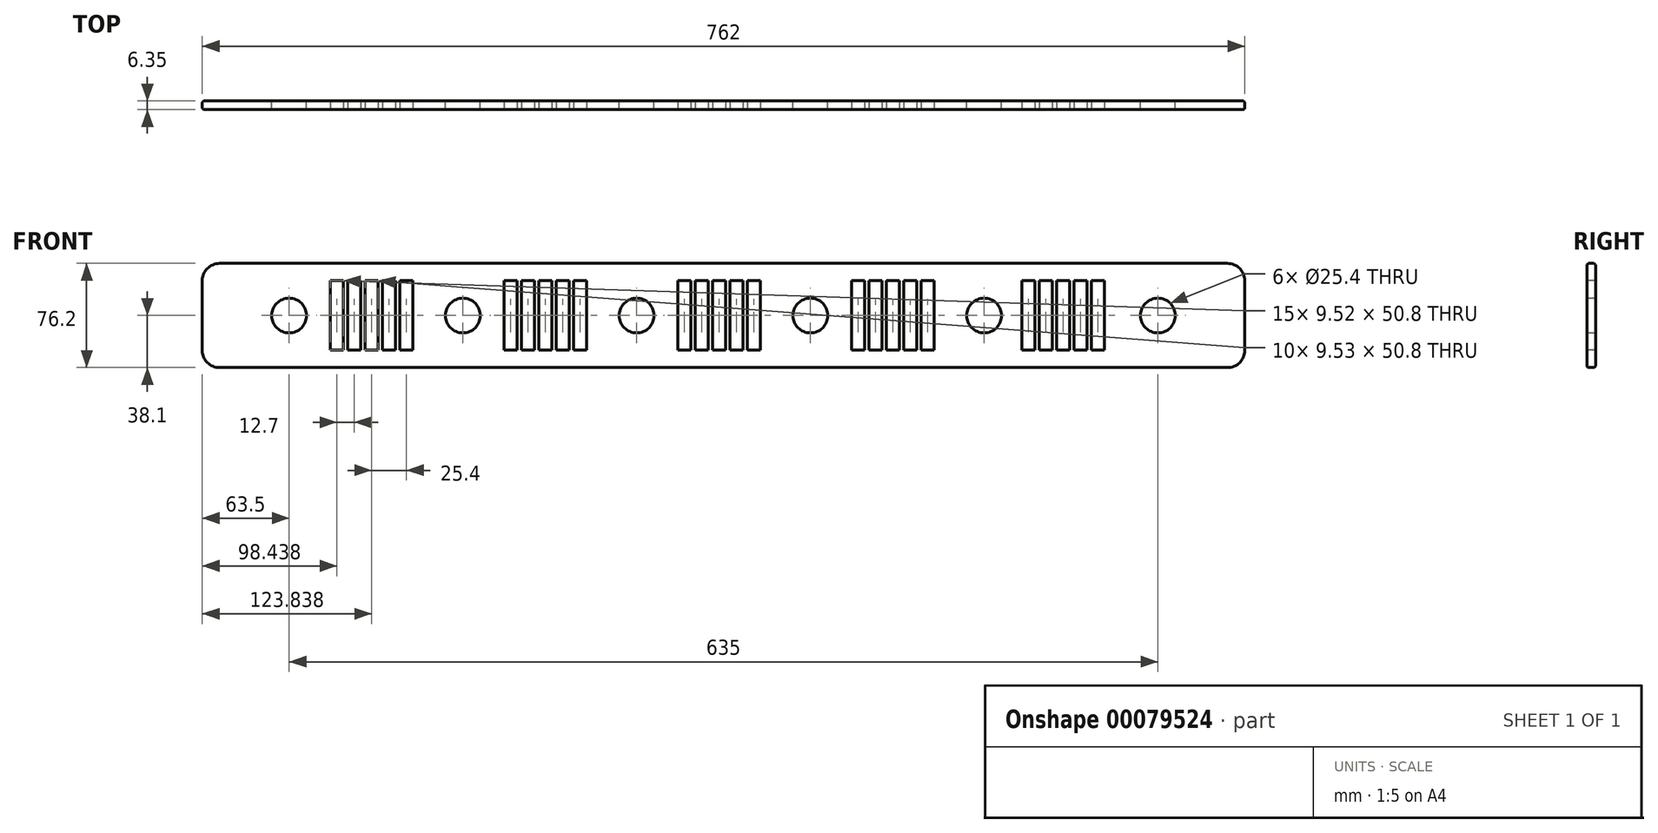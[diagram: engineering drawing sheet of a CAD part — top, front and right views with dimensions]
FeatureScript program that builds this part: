
annotation { "Feature Type Name" : "Feature", "Feature Type Description" : "" }
export const myFeature = defineFeature(function(context is Context, id is Id, definition is map)
    precondition{}
    {
        {
            var Q0;
            Q0=qCreatedBy(makeId("Front.planeOp"),FACE);
            var sketch = newSketch(context, id + "F0", { "sketchPlane" : qUnion([Q0])});
            skLineSegment(sketch, "E0.bottom", {"start": v(0, 0) * mm, "end": v(762, 0) * mm});
            skLineSegment(sketch, "E0.top", {"start": v(0, 76.2) * mm, "end": v(762, 76.2) * mm});
            skLineSegment(sketch, "E0.left", {"start": v(0, 0) * mm, "end": v(0, 76.2) * mm});
            skLineSegment(sketch, "E0.right", {"start": v(762, 0) * mm, "end": v(762, 76.2) * mm});
            skCircle(sketch, "E1", {"center": v(63.5, 38.1) * mm, "radius": 12.7 * mm});
            skPoint(sketch, "E1.centerSnap0", {"position": v(0, 38.1) * mm});
            skCircle(sketch, "E2", {"center": v(190.5, 38.1) * mm, "radius": 12.7 * mm});
            skCircle(sketch, "E3", {"center": v(317.5, 38.1) * mm, "radius": 12.7 * mm});
            skCircle(sketch, "E4", {"center": v(444.5, 38.1) * mm, "radius": 12.7 * mm});
            skCircle(sketch, "E5", {"center": v(571.5, 38.1) * mm, "radius": 12.7 * mm});
            skCircle(sketch, "E6", {"center": v(698.5, 38.1) * mm, "radius": 12.7 * mm});
            skSolve(sketch);
        }
        {
            var Q0;
            Q0=makeQuery(id+"F0.imprint","IMPRINT",FACE,{"disambiguationData":[TD([[makeQuery(id+"F0.imprint","IMPRINT",EDGE,{"derivedFrom":sQuery(id+"F0.wireOp",EDGE,"E0.bottom")}),1.0]])]});
            extrude(context, id + "F1", {"entities" : qUnion([Q0]), "depth" : 6.35 * mm});
        }
        {
            var Q0;
            Q0=makeQuery(id+"F1.opExtrude","CAP_FACE",FACE,{"disambiguationData":[OSD([sQuery(id+"F0.wireOp",EDGE,"E0.bottom"),sQuery(id+"F0.wireOp",EDGE,"E0.top"),sQuery(id+"F0.wireOp",EDGE,"E0.left"),sQuery(id+"F0.wireOp",EDGE,"E0.right"),sQuery(id+"F0.wireOp",EDGE,"E1"),sQuery(id+"F0.wireOp",EDGE,"E2"),sQuery(id+"F0.wireOp",EDGE,"E3"),sQuery(id+"F0.wireOp",EDGE,"E4"),sQuery(id+"F0.wireOp",EDGE,"E5"),sQuery(id+"F0.wireOp",EDGE,"E6")])],"isStart":false});
            var sketch = newSketch(context, id + "F2", { "sketchPlane" : qUnion([Q0])});
            skLineSegment(sketch, "E7.bottom", {"start": v(93.68, 63.5) * mm, "end": v(103.2, 63.5) * mm});
            skLineSegment(sketch, "E7.top", {"start": v(93.68, 12.7) * mm, "end": v(103.2, 12.7) * mm});
            skLineSegment(sketch, "E7.left", {"start": v(93.68, 63.5) * mm, "end": v(93.68, 12.7) * mm});
            skLineSegment(sketch, "E7.right", {"start": v(103.2, 63.5) * mm, "end": v(103.2, 12.7) * mm});
            skLineSegment(sketch, "E8.1.0.0", {"start": v(106.38, 63.5) * mm, "end": v(106.38, 12.7) * mm});
            skLineSegment(sketch, "E8.1.0.1", {"start": v(106.38, 63.5) * mm, "end": v(115.9, 63.5) * mm});
            skLineSegment(sketch, "E8.1.0.2", {"start": v(115.9, 63.5) * mm, "end": v(115.9, 12.7) * mm});
            skLineSegment(sketch, "E8.1.0.3", {"start": v(106.38, 12.7) * mm, "end": v(115.9, 12.7) * mm});
            skLineSegment(sketch, "E8.2.0.0", {"start": v(119.08, 63.5) * mm, "end": v(119.08, 12.7) * mm});
            skLineSegment(sketch, "E8.2.0.1", {"start": v(119.08, 63.5) * mm, "end": v(128.6, 63.5) * mm});
            skLineSegment(sketch, "E8.2.0.2", {"start": v(128.6, 63.5) * mm, "end": v(128.6, 12.7) * mm});
            skLineSegment(sketch, "E8.2.0.3", {"start": v(119.08, 12.7) * mm, "end": v(128.6, 12.7) * mm});
            skLineSegment(sketch, "E8.3.0.0", {"start": v(131.78, 63.5) * mm, "end": v(131.78, 12.7) * mm});
            skLineSegment(sketch, "E8.3.0.1", {"start": v(131.78, 63.5) * mm, "end": v(141.3, 63.5) * mm});
            skLineSegment(sketch, "E8.3.0.2", {"start": v(141.3, 63.5) * mm, "end": v(141.3, 12.7) * mm});
            skLineSegment(sketch, "E8.3.0.3", {"start": v(131.78, 12.7) * mm, "end": v(141.3, 12.7) * mm});
            skLineSegment(sketch, "E8.4.0.0", {"start": v(144.48, 63.5) * mm, "end": v(144.48, 12.7) * mm});
            skLineSegment(sketch, "E8.4.0.1", {"start": v(144.48, 63.5) * mm, "end": v(154, 63.5) * mm});
            skLineSegment(sketch, "E8.4.0.2", {"start": v(154, 63.5) * mm, "end": v(154, 12.7) * mm});
            skLineSegment(sketch, "E8.4.0.3", {"start": v(144.48, 12.7) * mm, "end": v(154, 12.7) * mm});
            skLineSegment(sketch, "E8.direction1", {"start": v(93.68, 12.7) * mm, "end": v(106.38, 12.7) * mm, "construction": true});
            skLineSegment(sketch, "E9.bottom", {"start": v(220.68, 63.5) * mm, "end": v(230.2, 63.5) * mm});
            skLineSegment(sketch, "E9.top", {"start": v(220.68, 12.7) * mm, "end": v(230.2, 12.7) * mm});
            skLineSegment(sketch, "E9.left", {"start": v(220.68, 63.5) * mm, "end": v(220.68, 12.7) * mm});
            skLineSegment(sketch, "E9.right", {"start": v(230.2, 63.5) * mm, "end": v(230.2, 12.7) * mm});
            skLineSegment(sketch, "E10.1.0.0", {"start": v(233.38, 63.5) * mm, "end": v(233.38, 12.7) * mm});
            skLineSegment(sketch, "E10.1.0.1", {"start": v(233.38, 63.5) * mm, "end": v(242.9, 63.5) * mm});
            skLineSegment(sketch, "E10.1.0.2", {"start": v(242.9, 63.5) * mm, "end": v(242.9, 12.7) * mm});
            skLineSegment(sketch, "E10.1.0.3", {"start": v(233.38, 12.7) * mm, "end": v(242.9, 12.7) * mm});
            skLineSegment(sketch, "E10.2.0.0", {"start": v(246.08, 63.5) * mm, "end": v(246.08, 12.7) * mm});
            skLineSegment(sketch, "E10.2.0.1", {"start": v(246.08, 63.5) * mm, "end": v(255.6, 63.5) * mm});
            skLineSegment(sketch, "E10.2.0.2", {"start": v(255.6, 63.5) * mm, "end": v(255.6, 12.7) * mm});
            skLineSegment(sketch, "E10.2.0.3", {"start": v(246.08, 12.7) * mm, "end": v(255.6, 12.7) * mm});
            skLineSegment(sketch, "E10.3.0.0", {"start": v(258.78, 63.5) * mm, "end": v(258.78, 12.7) * mm});
            skLineSegment(sketch, "E10.3.0.1", {"start": v(258.78, 63.5) * mm, "end": v(268.3, 63.5) * mm});
            skLineSegment(sketch, "E10.3.0.2", {"start": v(268.3, 63.5) * mm, "end": v(268.3, 12.7) * mm});
            skLineSegment(sketch, "E10.3.0.3", {"start": v(258.78, 12.7) * mm, "end": v(268.3, 12.7) * mm});
            skLineSegment(sketch, "E10.4.0.0", {"start": v(271.48, 63.5) * mm, "end": v(271.48, 12.7) * mm});
            skLineSegment(sketch, "E10.4.0.1", {"start": v(271.48, 63.5) * mm, "end": v(281, 63.5) * mm});
            skLineSegment(sketch, "E10.4.0.2", {"start": v(281, 63.5) * mm, "end": v(281, 12.7) * mm});
            skLineSegment(sketch, "E10.4.0.3", {"start": v(271.48, 12.7) * mm, "end": v(281, 12.7) * mm});
            skLineSegment(sketch, "E10.direction1", {"start": v(220.68, 12.7) * mm, "end": v(233.38, 12.7) * mm, "construction": true});
            skLineSegment(sketch, "E11.bottom", {"start": v(347.68, 63.5) * mm, "end": v(357.2, 63.5) * mm});
            skLineSegment(sketch, "E11.top", {"start": v(347.68, 12.7) * mm, "end": v(357.2, 12.7) * mm});
            skLineSegment(sketch, "E11.left", {"start": v(347.68, 63.5) * mm, "end": v(347.68, 12.7) * mm});
            skLineSegment(sketch, "E11.right", {"start": v(357.2, 63.5) * mm, "end": v(357.2, 12.7) * mm});
            skLineSegment(sketch, "E12.1.0.0", {"start": v(360.38, 63.5) * mm, "end": v(360.38, 12.7) * mm});
            skLineSegment(sketch, "E12.1.0.1", {"start": v(360.38, 63.5) * mm, "end": v(369.9, 63.5) * mm});
            skLineSegment(sketch, "E12.1.0.2", {"start": v(369.9, 63.5) * mm, "end": v(369.9, 12.7) * mm});
            skLineSegment(sketch, "E12.1.0.3", {"start": v(360.38, 12.7) * mm, "end": v(369.9, 12.7) * mm});
            skLineSegment(sketch, "E12.2.0.0", {"start": v(373.08, 63.5) * mm, "end": v(373.08, 12.7) * mm});
            skLineSegment(sketch, "E12.2.0.1", {"start": v(373.08, 63.5) * mm, "end": v(382.6, 63.5) * mm});
            skLineSegment(sketch, "E12.2.0.2", {"start": v(382.6, 63.5) * mm, "end": v(382.6, 12.7) * mm});
            skLineSegment(sketch, "E12.2.0.3", {"start": v(373.08, 12.7) * mm, "end": v(382.6, 12.7) * mm});
            skLineSegment(sketch, "E12.3.0.0", {"start": v(385.78, 63.5) * mm, "end": v(385.78, 12.7) * mm});
            skLineSegment(sketch, "E12.3.0.1", {"start": v(385.78, 63.5) * mm, "end": v(395.3, 63.5) * mm});
            skLineSegment(sketch, "E12.3.0.2", {"start": v(395.3, 63.5) * mm, "end": v(395.3, 12.7) * mm});
            skLineSegment(sketch, "E12.3.0.3", {"start": v(385.78, 12.7) * mm, "end": v(395.3, 12.7) * mm});
            skLineSegment(sketch, "E12.4.0.0", {"start": v(398.48, 63.5) * mm, "end": v(398.48, 12.7) * mm});
            skLineSegment(sketch, "E12.4.0.1", {"start": v(398.48, 63.5) * mm, "end": v(408, 63.5) * mm});
            skLineSegment(sketch, "E12.4.0.2", {"start": v(408, 63.5) * mm, "end": v(408, 12.7) * mm});
            skLineSegment(sketch, "E12.4.0.3", {"start": v(398.48, 12.7) * mm, "end": v(408, 12.7) * mm});
            skLineSegment(sketch, "E12.direction1", {"start": v(347.68, 12.7) * mm, "end": v(360.38, 12.7) * mm, "construction": true});
            skLineSegment(sketch, "E13.bottom", {"start": v(474.68, 63.5) * mm, "end": v(484.2, 63.5) * mm});
            skLineSegment(sketch, "E13.top", {"start": v(474.68, 12.7) * mm, "end": v(484.2, 12.7) * mm});
            skLineSegment(sketch, "E13.left", {"start": v(474.68, 63.5) * mm, "end": v(474.68, 12.7) * mm});
            skLineSegment(sketch, "E13.right", {"start": v(484.2, 63.5) * mm, "end": v(484.2, 12.7) * mm});
            skLineSegment(sketch, "E14.1.0.0", {"start": v(487.38, 63.5) * mm, "end": v(487.38, 12.7) * mm});
            skLineSegment(sketch, "E14.1.0.1", {"start": v(487.38, 63.5) * mm, "end": v(496.9, 63.5) * mm});
            skLineSegment(sketch, "E14.1.0.2", {"start": v(496.9, 63.5) * mm, "end": v(496.9, 12.7) * mm});
            skLineSegment(sketch, "E14.1.0.3", {"start": v(487.38, 12.7) * mm, "end": v(496.9, 12.7) * mm});
            skLineSegment(sketch, "E14.2.0.0", {"start": v(500.08, 63.5) * mm, "end": v(500.08, 12.7) * mm});
            skLineSegment(sketch, "E14.2.0.1", {"start": v(500.08, 63.5) * mm, "end": v(509.6, 63.5) * mm});
            skLineSegment(sketch, "E14.2.0.2", {"start": v(509.6, 63.5) * mm, "end": v(509.6, 12.7) * mm});
            skLineSegment(sketch, "E14.2.0.3", {"start": v(500.08, 12.7) * mm, "end": v(509.6, 12.7) * mm});
            skLineSegment(sketch, "E14.3.0.0", {"start": v(512.78, 63.5) * mm, "end": v(512.78, 12.7) * mm});
            skLineSegment(sketch, "E14.3.0.1", {"start": v(512.78, 63.5) * mm, "end": v(522.3, 63.5) * mm});
            skLineSegment(sketch, "E14.3.0.2", {"start": v(522.3, 63.5) * mm, "end": v(522.3, 12.7) * mm});
            skLineSegment(sketch, "E14.3.0.3", {"start": v(512.78, 12.7) * mm, "end": v(522.3, 12.7) * mm});
            skLineSegment(sketch, "E14.4.0.0", {"start": v(525.48, 63.5) * mm, "end": v(525.48, 12.7) * mm});
            skLineSegment(sketch, "E14.4.0.1", {"start": v(525.48, 63.5) * mm, "end": v(535, 63.5) * mm});
            skLineSegment(sketch, "E14.4.0.2", {"start": v(535, 63.5) * mm, "end": v(535, 12.7) * mm});
            skLineSegment(sketch, "E14.4.0.3", {"start": v(525.48, 12.7) * mm, "end": v(535, 12.7) * mm});
            skLineSegment(sketch, "E14.direction1", {"start": v(474.68, 12.7) * mm, "end": v(487.38, 12.7) * mm, "construction": true});
            skLineSegment(sketch, "E15.bottom", {"start": v(599.14, 63.5) * mm, "end": v(608.66, 63.5) * mm});
            skLineSegment(sketch, "E15.top", {"start": v(599.14, 12.7) * mm, "end": v(608.66, 12.7) * mm});
            skLineSegment(sketch, "E15.left", {"start": v(599.14, 63.5) * mm, "end": v(599.14, 12.7) * mm});
            skLineSegment(sketch, "E15.right", {"start": v(608.66, 63.5) * mm, "end": v(608.66, 12.7) * mm});
            skLineSegment(sketch, "E16.1.0.0", {"start": v(611.84, 63.5) * mm, "end": v(611.84, 12.7) * mm});
            skLineSegment(sketch, "E16.1.0.1", {"start": v(611.84, 63.5) * mm, "end": v(621.36, 63.5) * mm});
            skLineSegment(sketch, "E16.1.0.2", {"start": v(621.36, 63.5) * mm, "end": v(621.36, 12.7) * mm});
            skLineSegment(sketch, "E16.1.0.3", {"start": v(611.84, 12.7) * mm, "end": v(621.36, 12.7) * mm});
            skLineSegment(sketch, "E16.2.0.0", {"start": v(624.54, 63.5) * mm, "end": v(624.54, 12.7) * mm});
            skLineSegment(sketch, "E16.2.0.1", {"start": v(624.54, 63.5) * mm, "end": v(634.06, 63.5) * mm});
            skLineSegment(sketch, "E16.2.0.2", {"start": v(634.06, 63.5) * mm, "end": v(634.06, 12.7) * mm});
            skLineSegment(sketch, "E16.2.0.3", {"start": v(624.54, 12.7) * mm, "end": v(634.06, 12.7) * mm});
            skLineSegment(sketch, "E16.3.0.0", {"start": v(637.24, 63.5) * mm, "end": v(637.24, 12.7) * mm});
            skLineSegment(sketch, "E16.3.0.1", {"start": v(637.24, 63.5) * mm, "end": v(646.76, 63.5) * mm});
            skLineSegment(sketch, "E16.3.0.2", {"start": v(646.76, 63.5) * mm, "end": v(646.76, 12.7) * mm});
            skLineSegment(sketch, "E16.3.0.3", {"start": v(637.24, 12.7) * mm, "end": v(646.76, 12.7) * mm});
            skLineSegment(sketch, "E16.4.0.0", {"start": v(649.94, 63.5) * mm, "end": v(649.94, 12.7) * mm});
            skLineSegment(sketch, "E16.4.0.1", {"start": v(649.94, 63.5) * mm, "end": v(659.46, 63.5) * mm});
            skLineSegment(sketch, "E16.4.0.2", {"start": v(659.46, 63.5) * mm, "end": v(659.46, 12.7) * mm});
            skLineSegment(sketch, "E16.4.0.3", {"start": v(649.94, 12.7) * mm, "end": v(659.46, 12.7) * mm});
            skLineSegment(sketch, "E16.direction1", {"start": v(599.14, 12.7) * mm, "end": v(611.84, 12.7) * mm, "construction": true});
            skSolve(sketch);
        }
        {
            var Q0;
            Q0=makeQuery(id+"F2.imprint","IMPRINT",FACE,{"disambiguationData":[TD([[makeQuery(id+"F2.imprint","IMPRINT",EDGE,{"derivedFrom":sQuery(id+"F2.wireOp",EDGE,"E8.4.0.0")}),1.0]])]});
            var Q1;
            Q1=makeQuery(id+"F2.imprint","IMPRINT",FACE,{"disambiguationData":[TD([[makeQuery(id+"F2.imprint","IMPRINT",EDGE,{"derivedFrom":sQuery(id+"F2.wireOp",EDGE,"E8.3.0.0")}),1.0]])]});
            var Q2;
            Q2=makeQuery(id+"F2.imprint","IMPRINT",FACE,{"disambiguationData":[TD([[makeQuery(id+"F2.imprint","IMPRINT",EDGE,{"derivedFrom":sQuery(id+"F2.wireOp",EDGE,"E8.2.0.0")}),1.0]])]});
            var Q3;
            Q3=makeQuery(id+"F2.imprint","IMPRINT",FACE,{"disambiguationData":[TD([[makeQuery(id+"F2.imprint","IMPRINT",EDGE,{"derivedFrom":sQuery(id+"F2.wireOp",EDGE,"E8.1.0.0")}),1.0]])]});
            var Q4;
            Q4=makeQuery(id+"F2.imprint","IMPRINT",FACE,{"disambiguationData":[TD([[makeQuery(id+"F2.imprint","IMPRINT",EDGE,{"derivedFrom":sQuery(id+"F2.wireOp",EDGE,"E7.bottom")}),-1.0]])]});
            var Q5;
            Q5=makeQuery(id+"F2.imprint","IMPRINT",FACE,{"disambiguationData":[TD([[makeQuery(id+"F2.imprint","IMPRINT",EDGE,{"derivedFrom":sQuery(id+"F2.wireOp",EDGE,"E9.bottom")}),-1.0]])]});
            var Q6;
            Q6=makeQuery(id+"F2.imprint","IMPRINT",FACE,{"disambiguationData":[TD([[makeQuery(id+"F2.imprint","IMPRINT",EDGE,{"derivedFrom":sQuery(id+"F2.wireOp",EDGE,"E10.1.0.0")}),1.0]])]});
            var Q7;
            Q7=makeQuery(id+"F2.imprint","IMPRINT",FACE,{"disambiguationData":[TD([[makeQuery(id+"F2.imprint","IMPRINT",EDGE,{"derivedFrom":sQuery(id+"F2.wireOp",EDGE,"E10.2.0.0")}),1.0]])]});
            var Q8;
            Q8=makeQuery(id+"F2.imprint","IMPRINT",FACE,{"disambiguationData":[TD([[makeQuery(id+"F2.imprint","IMPRINT",EDGE,{"derivedFrom":sQuery(id+"F2.wireOp",EDGE,"E10.3.0.0")}),1.0]])]});
            var Q9;
            Q9=makeQuery(id+"F2.imprint","IMPRINT",FACE,{"disambiguationData":[TD([[makeQuery(id+"F2.imprint","IMPRINT",EDGE,{"derivedFrom":sQuery(id+"F2.wireOp",EDGE,"E10.4.0.0")}),1.0]])]});
            var Q10;
            Q10=makeQuery(id+"F2.imprint","IMPRINT",FACE,{"disambiguationData":[TD([[makeQuery(id+"F2.imprint","IMPRINT",EDGE,{"derivedFrom":sQuery(id+"F2.wireOp",EDGE,"E11.bottom")}),-1.0]])]});
            var Q11;
            Q11=makeQuery(id+"F2.imprint","IMPRINT",FACE,{"disambiguationData":[TD([[makeQuery(id+"F2.imprint","IMPRINT",EDGE,{"derivedFrom":sQuery(id+"F2.wireOp",EDGE,"E12.1.0.0")}),1.0]])]});
            var Q12;
            Q12=makeQuery(id+"F2.imprint","IMPRINT",FACE,{"disambiguationData":[TD([[makeQuery(id+"F2.imprint","IMPRINT",EDGE,{"derivedFrom":sQuery(id+"F2.wireOp",EDGE,"E12.2.0.0")}),1.0]])]});
            var Q13;
            Q13=makeQuery(id+"F2.imprint","IMPRINT",FACE,{"disambiguationData":[TD([[makeQuery(id+"F2.imprint","IMPRINT",EDGE,{"derivedFrom":sQuery(id+"F2.wireOp",EDGE,"E12.3.0.0")}),1.0]])]});
            var Q14;
            Q14=makeQuery(id+"F2.imprint","IMPRINT",FACE,{"disambiguationData":[TD([[makeQuery(id+"F2.imprint","IMPRINT",EDGE,{"derivedFrom":sQuery(id+"F2.wireOp",EDGE,"E12.4.0.0")}),1.0]])]});
            var Q15;
            Q15=makeQuery(id+"F2.imprint","IMPRINT",FACE,{"disambiguationData":[TD([[makeQuery(id+"F2.imprint","IMPRINT",EDGE,{"derivedFrom":sQuery(id+"F2.wireOp",EDGE,"E13.bottom")}),-1.0]])]});
            var Q16;
            Q16=makeQuery(id+"F2.imprint","IMPRINT",FACE,{"disambiguationData":[TD([[makeQuery(id+"F2.imprint","IMPRINT",EDGE,{"derivedFrom":sQuery(id+"F2.wireOp",EDGE,"E14.1.0.0")}),1.0]])]});
            var Q17;
            Q17=makeQuery(id+"F2.imprint","IMPRINT",FACE,{"disambiguationData":[TD([[makeQuery(id+"F2.imprint","IMPRINT",EDGE,{"derivedFrom":sQuery(id+"F2.wireOp",EDGE,"E14.2.0.0")}),1.0]])]});
            var Q18;
            Q18=makeQuery(id+"F2.imprint","IMPRINT",FACE,{"disambiguationData":[TD([[makeQuery(id+"F2.imprint","IMPRINT",EDGE,{"derivedFrom":sQuery(id+"F2.wireOp",EDGE,"E14.3.0.0")}),1.0]])]});
            var Q19;
            Q19=makeQuery(id+"F2.imprint","IMPRINT",FACE,{"disambiguationData":[TD([[makeQuery(id+"F2.imprint","IMPRINT",EDGE,{"derivedFrom":sQuery(id+"F2.wireOp",EDGE,"E14.4.0.0")}),1.0]])]});
            var Q20;
            Q20=makeQuery(id+"F2.imprint","IMPRINT",FACE,{"disambiguationData":[TD([[makeQuery(id+"F2.imprint","IMPRINT",EDGE,{"derivedFrom":sQuery(id+"F2.wireOp",EDGE,"E15.bottom")}),-1.0]])]});
            var Q21;
            Q21=makeQuery(id+"F2.imprint","IMPRINT",FACE,{"disambiguationData":[TD([[makeQuery(id+"F2.imprint","IMPRINT",EDGE,{"derivedFrom":sQuery(id+"F2.wireOp",EDGE,"E16.1.0.0")}),1.0]])]});
            var Q22;
            Q22=makeQuery(id+"F2.imprint","IMPRINT",FACE,{"disambiguationData":[TD([[makeQuery(id+"F2.imprint","IMPRINT",EDGE,{"derivedFrom":sQuery(id+"F2.wireOp",EDGE,"E16.2.0.0")}),1.0]])]});
            var Q23;
            Q23=makeQuery(id+"F2.imprint","IMPRINT",FACE,{"disambiguationData":[TD([[makeQuery(id+"F2.imprint","IMPRINT",EDGE,{"derivedFrom":sQuery(id+"F2.wireOp",EDGE,"E16.4.0.0")}),1.0]])]});
            var Q24;
            Q24=makeQuery(id+"F2.imprint","IMPRINT",FACE,{"disambiguationData":[TD([[makeQuery(id+"F2.imprint","IMPRINT",EDGE,{"derivedFrom":sQuery(id+"F2.wireOp",EDGE,"E16.3.0.0")}),1.0]])]});
            extrude(context, id + "F3", {"entities" : qUnion([Q0, Q1, Q2, Q3, Q4, Q5, Q6, Q7, Q8, Q9, Q10, Q11, Q12, Q13, Q14, Q15, Q16, Q17, Q18, Q19, Q20, Q21, Q22, Q23, Q24]), "operationType" : NewBodyOperationType.REMOVE, "endBound" : BoundingType.THROUGH_ALL, "oppositeDirection" : true, "depth" : 25.4 * mm});
        }
        {
            var Q0;
            Q0=makeQuery(id+"F1.opExtrude","SWEPT_EDGE",EDGE,{"disambiguationData":[OSD([sQuery(id+"F0.wireOp",EDGE,"E0.top"),sQuery(id+"F0.wireOp",EDGE,"E0.left")])]});
            var Q1;
            Q1=makeQuery(id+"F1.opExtrude","SWEPT_EDGE",EDGE,{"disambiguationData":[OSD([sQuery(id+"F0.wireOp",EDGE,"E0.bottom"),sQuery(id+"F0.wireOp",EDGE,"E0.left")])]});
            var Q2;
            Q2=makeQuery(id+"F1.opExtrude","SWEPT_EDGE",EDGE,{"disambiguationData":[OSD([sQuery(id+"F0.wireOp",EDGE,"E0.top"),sQuery(id+"F0.wireOp",EDGE,"E0.right")])]});
            var Q3;
            Q3=makeQuery(id+"F1.opExtrude","SWEPT_EDGE",EDGE,{"disambiguationData":[OSD([sQuery(id+"F0.wireOp",EDGE,"E0.bottom"),sQuery(id+"F0.wireOp",EDGE,"E0.right")])]});
            fillet(context, id + "F4", {"entities" : qUnion([Q0, Q1, Q2, Q3]), "radius" : 12.7 * mm, "tangentPropagation" : true, "allowEdgeOverflow" : false});
        }
        {
            var Q0;
            Q0=makeQuery(id+"F1.opExtrude","CAP_EDGE",EDGE,{"disambiguationData":[OSD([sQuery(id+"F0.wireOp",EDGE,"E0.top")])],"isStart":false});
            var Q1;
            Q1=makeQuery(id+"F1.opExtrude","CAP_EDGE",EDGE,{"disambiguationData":[OSD([sQuery(id+"F0.wireOp",EDGE,"E0.top")])],"isStart":true});
            fillet(context, id + "F5", {"entities" : qUnion([Q0, Q1]), "radius" : 1.6 * mm, "tangentPropagation" : true, "allowEdgeOverflow" : false});
        }
    });
